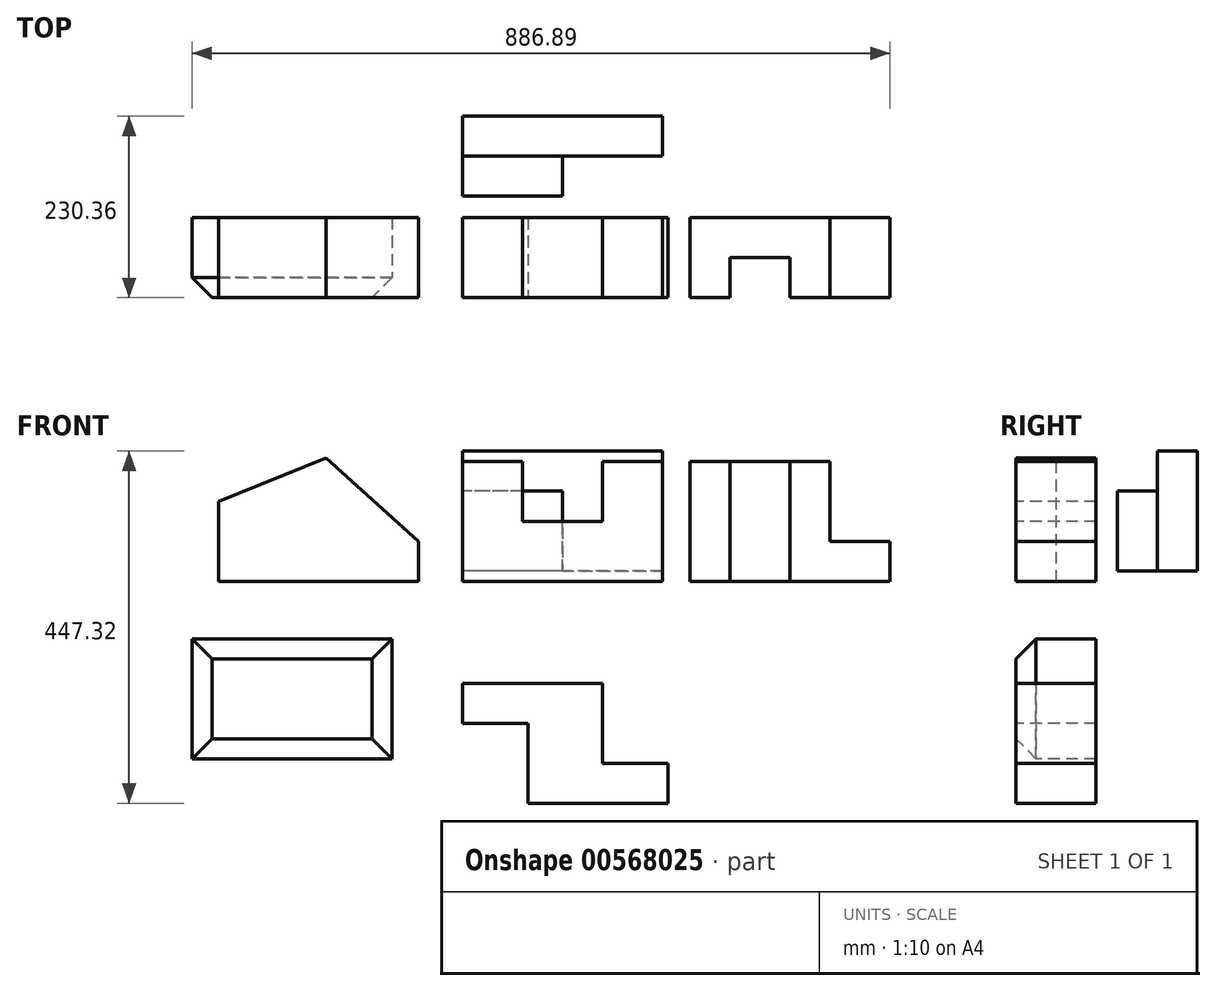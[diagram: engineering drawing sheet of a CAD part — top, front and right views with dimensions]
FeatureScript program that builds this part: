
annotation { "Feature Type Name" : "Feature", "Feature Type Description" : "" }
export const myFeature = defineFeature(function(context is Context, id is Id, definition is map)
    precondition{}
    {
        {
            var Q0;
            Q0=qCreatedBy(makeId("Front.planeOp"),FACE);
            var sketch = newSketch(context, id + "F0", { "sketchPlane" : qUnion([Q0])});
            skLineSegment(sketch, "E0", {"start": v(0, 0) * mm, "end": v(0, 152.4) * mm});
            skLineSegment(sketch, "E1", {"start": v(0, 152.4) * mm, "end": v(76.2, 152.4) * mm});
            skLineSegment(sketch, "E2", {"start": v(76.2, 152.4) * mm, "end": v(76.2, 76.2) * mm});
            skLineSegment(sketch, "E3", {"start": v(76.2, 76.2) * mm, "end": v(177.8, 76.2) * mm});
            skLineSegment(sketch, "E4", {"start": v(177.8, 76.2) * mm, "end": v(177.8, 152.4) * mm});
            skLineSegment(sketch, "E5", {"start": v(177.8, 152.4) * mm, "end": v(254, 152.4) * mm});
            skLineSegment(sketch, "E6", {"start": v(254, 152.4) * mm, "end": v(254, 0) * mm});
            skLineSegment(sketch, "E7", {"start": v(254, 0) * mm, "end": v(0, 0) * mm});
            skSolve(sketch);
        }
        {
            var Q0;
            Q0=makeQuery(id+"F0.imprint","IMPRINT",FACE,{"disambiguationData":[TD([[makeQuery(id+"F0.imprint","IMPRINT",EDGE,{"derivedFrom":sQuery(id+"F0.wireOp",EDGE,"E0")}),-1.0]])]});
            extrude(context, id + "F1", {"entities" : qUnion([Q0]), "oppositeDirection" : true, "depth" : 101.6 * mm, "offsetDistance" : 25.4 * mm});
        }
        {
            var Q0;
            Q0=qCreatedBy(makeId("Right.planeOp"),FACE);
            var sketch = newSketch(context, id + "F2", { "sketchPlane" : qUnion([Q0])});
            skLineSegment(sketch, "E8", {"start": v(230.36, 165.4) * mm, "end": v(230.36, 13) * mm});
            skLineSegment(sketch, "E9", {"start": v(230.36, 13) * mm, "end": v(128.76, 13) * mm});
            skLineSegment(sketch, "E10", {"start": v(128.76, 13) * mm, "end": v(128.76, 114.6) * mm});
            skLineSegment(sketch, "E11", {"start": v(128.76, 114.6) * mm, "end": v(179.56, 114.6) * mm});
            skLineSegment(sketch, "E12", {"start": v(179.56, 114.6) * mm, "end": v(179.56, 165.4) * mm});
            skLineSegment(sketch, "E13", {"start": v(179.56, 165.4) * mm, "end": v(230.36, 165.4) * mm});
            skSolve(sketch);
        }
        {
            var Q0;
            Q0=makeQuery(id+"F2.imprint","IMPRINT",FACE,{"disambiguationData":[TD([[makeQuery(id+"F2.imprint","IMPRINT",EDGE,{"derivedFrom":sQuery(id+"F2.wireOp",EDGE,"E8")}),-1.0]])]});
            extrude(context, id + "F3", {"entities" : qUnion([Q0]), "depth" : 254 * mm, "offsetDistance" : 25.4 * mm});
        }
        {
            var Q0;
            Q0=makeQuery(id+"F3.opExtrude","CAP_FACE",FACE,{"disambiguationData":[OSD([sQuery(id+"F2.wireOp",EDGE,"E8"),sQuery(id+"F2.wireOp",EDGE,"E9"),sQuery(id+"F2.wireOp",EDGE,"E10"),sQuery(id+"F2.wireOp",EDGE,"E11"),sQuery(id+"F2.wireOp",EDGE,"E12"),sQuery(id+"F2.wireOp",EDGE,"E13")])],"isStart":false});
            var sketch = newSketch(context, id + "F4", { "sketchPlane" : qUnion([Q0])});
            skLineSegment(sketch, "E14", {"start": v(128.76, 114.6) * mm, "end": v(179.56, 114.6) * mm});
            skLineSegment(sketch, "E15", {"start": v(179.56, 114.6) * mm, "end": v(179.56, 13) * mm});
            skLineSegment(sketch, "E16", {"start": v(179.56, 13) * mm, "end": v(128.76, 13) * mm});
            skLineSegment(sketch, "E17", {"start": v(128.76, 13) * mm, "end": v(128.76, 114.6) * mm});
            skSolve(sketch);
        }
        {
            var Q0;
            Q0=makeQuery(id+"F4.imprint","IMPRINT",FACE,{"disambiguationData":[TD([[makeQuery(id+"F4.imprint","IMPRINT",EDGE,{"derivedFrom":sQuery(id+"F4.wireOp",EDGE,"E14")}),-1.0]])]});
            extrude(context, id + "F5", {"entities" : qUnion([Q0]), "operationType" : NewBodyOperationType.REMOVE, "oppositeDirection" : true, "depth" : 127 * mm, "offsetDistance" : 25.4 * mm});
        }
        {
            var Q0;
            Q0=qCreatedBy(makeId("Top.planeOp"),FACE);
            var sketch = newSketch(context, id + "F6", { "sketchPlane" : qUnion([Q0])});
            skLineSegment(sketch, "E18", {"start": v(543.41, 0) * mm, "end": v(543.41, 101.6) * mm});
            skLineSegment(sketch, "E19", {"start": v(543.41, 101.6) * mm, "end": v(289.41, 101.6) * mm});
            skLineSegment(sketch, "E20", {"start": v(289.41, 101.6) * mm, "end": v(289.41, 0) * mm});
            skLineSegment(sketch, "E21", {"start": v(289.41, 0) * mm, "end": v(340.21, 0) * mm});
            skLineSegment(sketch, "E22", {"start": v(340.21, 0) * mm, "end": v(340.21, 50.8) * mm});
            skPoint(sketch, "E22.endSnap0", {"position": v(289.41, 50.8) * mm});
            skLineSegment(sketch, "E23", {"start": v(340.21, 50.8) * mm, "end": v(416.41, 50.8) * mm});
            skLineSegment(sketch, "E24", {"start": v(416.41, 50.8) * mm, "end": v(416.41, 0) * mm});
            skLineSegment(sketch, "E25", {"start": v(467.21, 0) * mm, "end": v(467.21, 101.6) * mm});
            skLineSegment(sketch, "E26", {"start": v(416.41, 0) * mm, "end": v(543.41, 0) * mm});
            skSolve(sketch);
        }
        {
            var Q0;
            {var subQ0=sQuery(id+"F6.wireOp",EDGE,"E20");Q0=makeQuery(id+"F6.imprint","IMPRINT",FACE,{"disambiguationData":[TD([[makeQuery(id+"F6.imprint","IMPRINT",EDGE,{"derivedFrom":subQ0}),1.0]])]});}
            extrude(context, id + "F7", {"entities" : qUnion([Q0]), "depth" : 152.4 * mm, "offsetDistance" : 25.4 * mm});
        }
        {
            var Q0;
            Q0 = qSketchRegion(id + "F6", true);
            extrude(context, id + "F8", {"entities" : qUnion([Q0]), "operationType" : NewBodyOperationType.ADD, "depth" : 50.8 * mm, "offsetDistance" : 25.4 * mm});
        }
        {
            var Q0;
            Q0=qCreatedBy(makeId("Front.planeOp"),FACE);
            var sketch = newSketch(context, id + "F9", { "sketchPlane" : qUnion([Q0])});
            skLineSegment(sketch, "E27", {"start": v(0, -129.52) * mm, "end": v(177.8, -129.52) * mm});
            skLineSegment(sketch, "E28", {"start": v(177.8, -129.52) * mm, "end": v(177.8, -231.12) * mm});
            skLineSegment(sketch, "E29", {"start": v(177.8, -231.12) * mm, "end": v(261, -231.12) * mm});
            skLineSegment(sketch, "E30", {"start": v(261, -231.12) * mm, "end": v(261, -281.92) * mm});
            skLineSegment(sketch, "E31", {"start": v(261, -281.92) * mm, "end": v(83.2, -281.92) * mm});
            skLineSegment(sketch, "E32", {"start": v(83.2, -281.92) * mm, "end": v(83.2, -180.32) * mm});
            skLineSegment(sketch, "E33", {"start": v(83.2, -180.32) * mm, "end": v(0, -180.32) * mm});
            skLineSegment(sketch, "E34", {"start": v(0, -180.32) * mm, "end": v(0, -129.52) * mm});
            skSolve(sketch);
        }
        {
            var Q0;
            Q0=makeQuery(id+"F9.imprint","IMPRINT",FACE,{"disambiguationData":[TD([[makeQuery(id+"F9.imprint","IMPRINT",EDGE,{"derivedFrom":sQuery(id+"F9.wireOp",EDGE,"E27")}),-1.0]])]});
            extrude(context, id + "F10", {"entities" : qUnion([Q0]), "oppositeDirection" : true, "depth" : 101.6 * mm, "offsetDistance" : 25.4 * mm});
        }
        {
            var Q0;
            Q0=qCreatedBy(makeId("Front.planeOp"),FACE);
            var sketch = newSketch(context, id + "F11", { "sketchPlane" : qUnion([Q0])});
            skLineSegment(sketch, "E35", {"start": v(-55.66, 0) * mm, "end": v(-309.66, 0) * mm});
            skLineSegment(sketch, "E36", {"start": v(-309.66, 0) * mm, "end": v(-309.66, 101.6) * mm});
            skPoint(sketch, "E37.endSnap0", {"position": v(-309.66, 50.8) * mm});
            skLineSegment(sketch, "E38", {"start": v(-173.38, 156.97) * mm, "end": v(-309.66, 101.6) * mm});
            skLineSegment(sketch, "E39", {"start": v(-55.66, 0) * mm, "end": v(-55.66, 50.8) * mm});
            skLineSegment(sketch, "E40", {"start": v(-55.66, 50.8) * mm, "end": v(-173.38, 156.97) * mm});
            skSolve(sketch);
        }
        {
            var Q0;
            Q0=makeQuery(id+"F11.imprint","IMPRINT",FACE,{"disambiguationData":[TD([[makeQuery(id+"F11.imprint","IMPRINT",EDGE,{"derivedFrom":sQuery(id+"F11.wireOp",EDGE,"E35")}),-1.0]])]});
            extrude(context, id + "F12", {"entities" : qUnion([Q0]), "oppositeDirection" : true, "depth" : 101.6 * mm, "offsetDistance" : 25.4 * mm});
        }
        {
            var Q0;
            Q0=qCreatedBy(makeId("Front.planeOp"),FACE);
            var sketch = newSketch(context, id + "F13", { "sketchPlane" : qUnion([Q0])});
            skLineSegment(sketch, "E41", {"start": v(-89.48, -73.1) * mm, "end": v(-343.48, -73.1) * mm});
            skLineSegment(sketch, "E42", {"start": v(-343.48, -73.1) * mm, "end": v(-343.48, -225.5) * mm});
            skLineSegment(sketch, "E43", {"start": v(-343.48, -225.5) * mm, "end": v(-89.48, -225.5) * mm});
            skLineSegment(sketch, "E44", {"start": v(-89.48, -225.5) * mm, "end": v(-89.48, -73.1) * mm});
            skLineSegment(sketch, "E45", {"start": v(-323.67, -195.4) * mm, "end": v(-120.47, -195.4) * mm});
            skLineSegment(sketch, "E46", {"start": v(-120.47, -195.4) * mm, "end": v(-120.47, -93.8) * mm});
            skLineSegment(sketch, "E47", {"start": v(-120.47, -93.8) * mm, "end": v(-323.67, -93.8) * mm});
            skLineSegment(sketch, "E48", {"start": v(-323.67, -93.8) * mm, "end": v(-323.67, -195.4) * mm});
            skSolve(sketch);
        }
        {
            var Q0;
            Q0=makeQuery(id+"F13.imprint","IMPRINT",FACE,{"disambiguationData":[TD([[makeQuery(id+"F13.imprint","IMPRINT",EDGE,{"derivedFrom":sQuery(id+"F13.wireOp",EDGE,"E41")}),1.0]])]});
            var Q1;
            Q1=makeQuery(id+"F13.imprint","IMPRINT",FACE,{"disambiguationData":[TD([[makeQuery(id+"F13.imprint","IMPRINT",EDGE,{"derivedFrom":sQuery(id+"F13.wireOp",EDGE,"E45")}),1.0]])]});
            extrude(context, id + "F14", {"entities" : qUnion([Q0, Q1]), "oppositeDirection" : true, "depth" : 101.6 * mm, "offsetDistance" : 25.4 * mm});
        }
        {
            var Q0;
            Q0=makeQuery(id+"F14.opExtrude","CAP_FACE",FACE,{"disambiguationData":[OSD([sQuery(id+"F13.wireOp",EDGE,"E41"),sQuery(id+"F13.wireOp",EDGE,"E42"),sQuery(id+"F13.wireOp",EDGE,"E43"),sQuery(id+"F13.wireOp",EDGE,"E44")])],"isStart":true});
            chamfer(context, id + "F15", {"entities" : qUnion([Q0]), "width" : 25.4 * mm, "tangentPropagation" : true});
        }
    });
